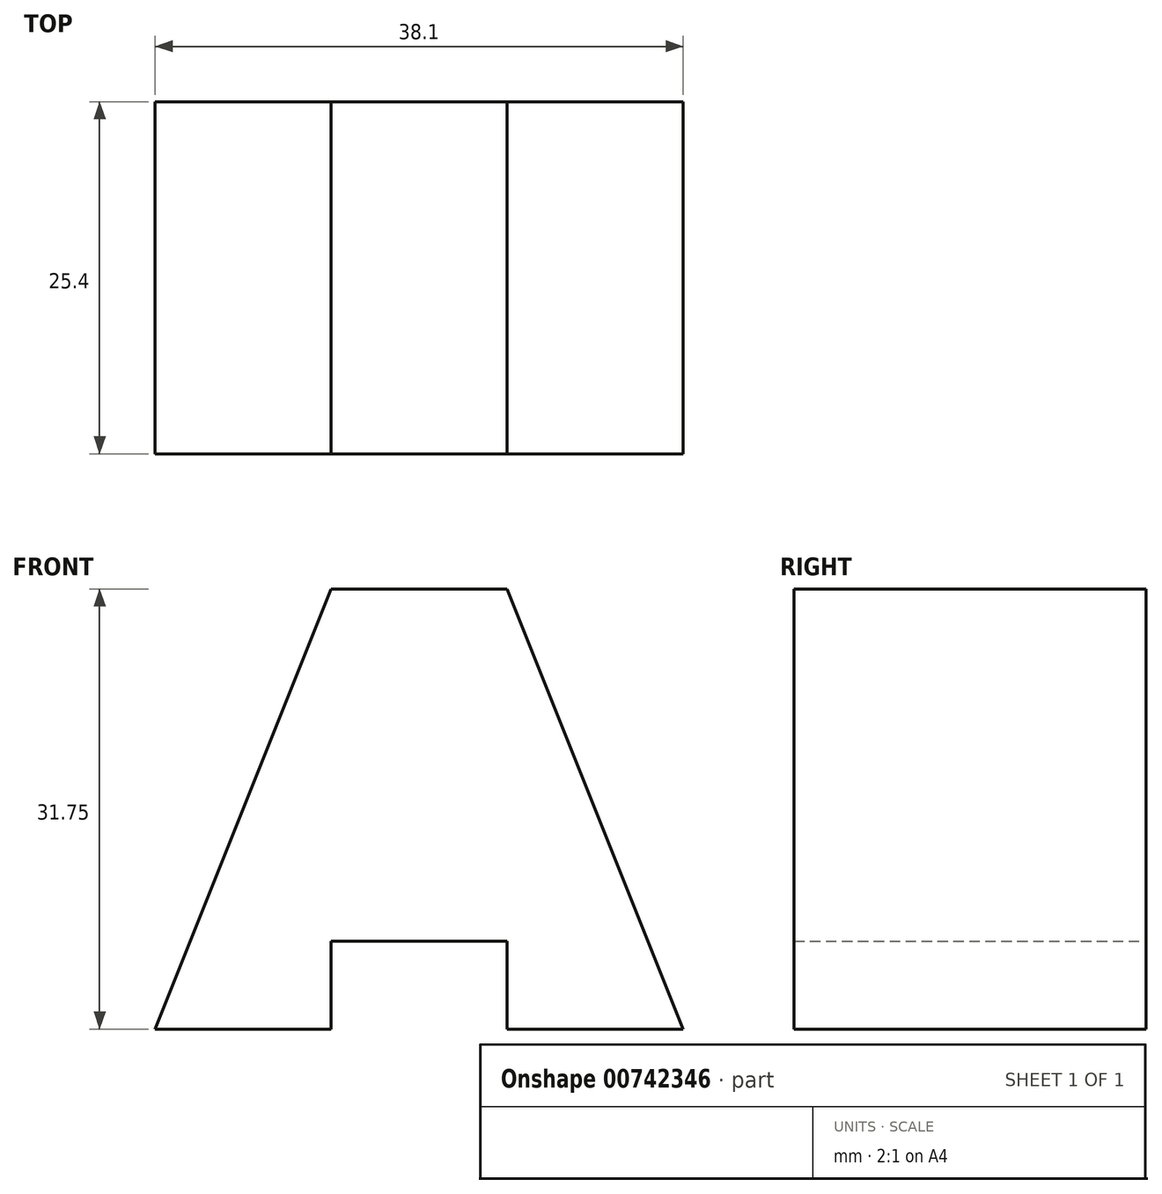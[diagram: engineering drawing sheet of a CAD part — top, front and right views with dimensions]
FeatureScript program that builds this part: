
annotation { "Feature Type Name" : "Feature", "Feature Type Description" : "" }
export const myFeature = defineFeature(function(context is Context, id is Id, definition is map)
    precondition{}
    {
        {
            var Q0;
            Q0=qCreatedBy(makeId("Front.planeOp"),FACE);
            var sketch = newSketch(context, id + "F0", { "sketchPlane" : qUnion([Q0])});
            skLineSegment(sketch, "E0", {"start": v(0, 0) * mm, "end": v(0, 31.75) * mm});
            skLineSegment(sketch, "E1", {"start": v(0, 31.75) * mm, "end": v(38.1, 31.75) * mm});
            skLineSegment(sketch, "E2", {"start": v(38.1, 31.75) * mm, "end": v(38.1, 0) * mm});
            skLineSegment(sketch, "E3", {"start": v(38.1, 0) * mm, "end": v(25.4, 0) * mm});
            skLineSegment(sketch, "E4", {"start": v(25.4, 0) * mm, "end": v(25.4, 6.35) * mm});
            skLineSegment(sketch, "E5", {"start": v(25.4, 6.35) * mm, "end": v(12.7, 6.35) * mm});
            skLineSegment(sketch, "E6", {"start": v(12.7, 6.35) * mm, "end": v(12.7, 0) * mm});
            skLineSegment(sketch, "E7", {"start": v(12.7, 0) * mm, "end": v(0, 0) * mm});
            skLineSegment(sketch, "E8", {"start": v(0, 0) * mm, "end": v(12.7, 31.75) * mm});
            skLineSegment(sketch, "E9", {"start": v(38.1, 0) * mm, "end": v(25.4, 31.75) * mm});
            skSolve(sketch);
        }
        {
            var Q0;
            Q0=makeQuery(id+"F0.imprint","IMPRINT",FACE,{"disambiguationData":[TD([[makeQuery(id+"F0.imprint","IMPRINT",EDGE,{"derivedFrom":sQuery(id+"F0.wireOp",EDGE,"E3")}),-1.0]])]});
            extrude(context, id + "F1", {"entities" : qUnion([Q0]), "depth" : 25.4 * mm, "offsetDistance" : 25.4 * mm});
        }
    });
